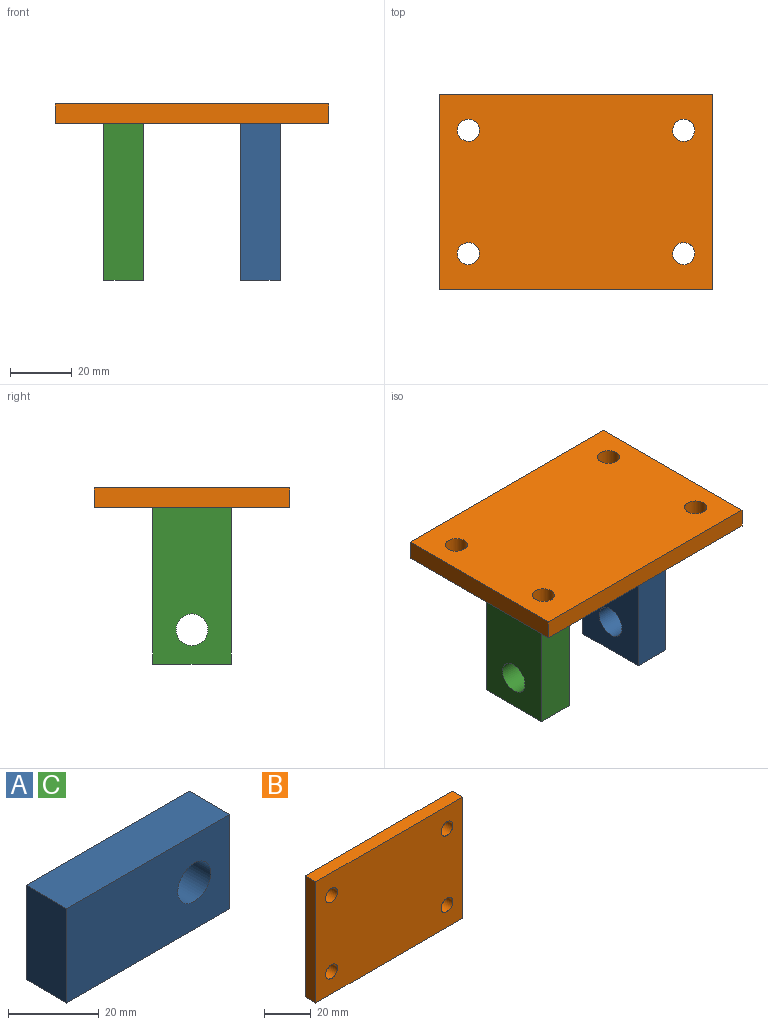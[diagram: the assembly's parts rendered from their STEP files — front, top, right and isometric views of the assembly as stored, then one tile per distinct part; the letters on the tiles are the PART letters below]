
ASSEMBLY  parts=3 mates=2
PART A: 7 faces, bbox 50.8x12.7x25.4 mm
  f0: plane 25.4x12.7mm, normal (-1,0,0), area 322.6mm2, adj f1,f4,f5,f6
  f1: plane 50.8x12.7mm, normal (0,0,-1), area 645.2mm2, adj f0,f2,f5,f6
  f2: plane 25.4x12.7mm, normal (1,0,0), area 322.6mm2, adj f1,f4,f5,f6
  f3: cylinder r=5.16mm len=12.7mm, axis (0,1,0), area 411.4mm2, adj f5,f6
  f4: plane 50.8x12.7mm, normal (0,0,1), area 645.2mm2, adj f0,f2,f5,f6
  f5: plane 50.8x25.4mm, normal (0,-1,0), area 1206.8mm2, adj f0,f1,f2,f3,f4
  f6: plane 50.8x25.4mm, normal (0,1,0), area 1206.8mm2, adj f0,f1,f2,f3,f4
PART B: 10 faces, bbox 88.9x6.4x63.5 mm
  f0: plane 63.5x6.35mm, normal (-1,0,0), area 403.2mm2, adj f1,f7,f8,f9
  f1: plane 88.9x6.35mm, normal (0,0,-1), area 564.5mm2, adj f0,f2,f8,f9
  f2: plane 63.5x6.35mm, normal (1,0,0), area 403.2mm2, adj f1,f7,f8,f9
  f3: cylinder r=3.57mm len=7.14mm, axis (0,1,0), area 142.4mm2, adj f8,f9
  f4: cylinder r=3.57mm len=7.14mm, axis (0,1,0), area 142.4mm2, adj f8,f9
  f5: cylinder r=3.57mm len=7.14mm, axis (0,1,0), area 142.4mm2, adj f8,f9
  f6: cylinder r=3.57mm len=7.14mm, axis (0,1,0), area 142.4mm2, adj f8,f9
  f7: plane 88.9x6.35mm, normal (0,0,1), area 564.5mm2, adj f0,f2,f8,f9
  f8: plane 88.9x63.5mm, normal (0,-1,0), area 5485.1mm2, adj f0,f1,f2,f3,f4,f5,f6,f7
  f9: plane 88.9x63.5mm, normal (0,1,0), area 5485.1mm2, adj f0,f1,f2,f3,f4,f5,f6,f7
PART C: same geometry as A
PLACE A rot(axis=(0.58,0.58,-0.58),120deg) t=(22.23,0,-25.4)mm
PLACE B rot(axis=(1,0,0),90deg) t=(0,0,3.17)mm
PLACE C rot(axis=(0.58,0.58,-0.58),120deg) t=(-22.23,0,-25.4)mm
MATE fastened A.f0 <-> B.f8  axis (0,0,1) through (22.23,0,0)mm
MATE fastened B.f8 <-> C.f0  axis (0,0,-1) through (0,0,0)mm
